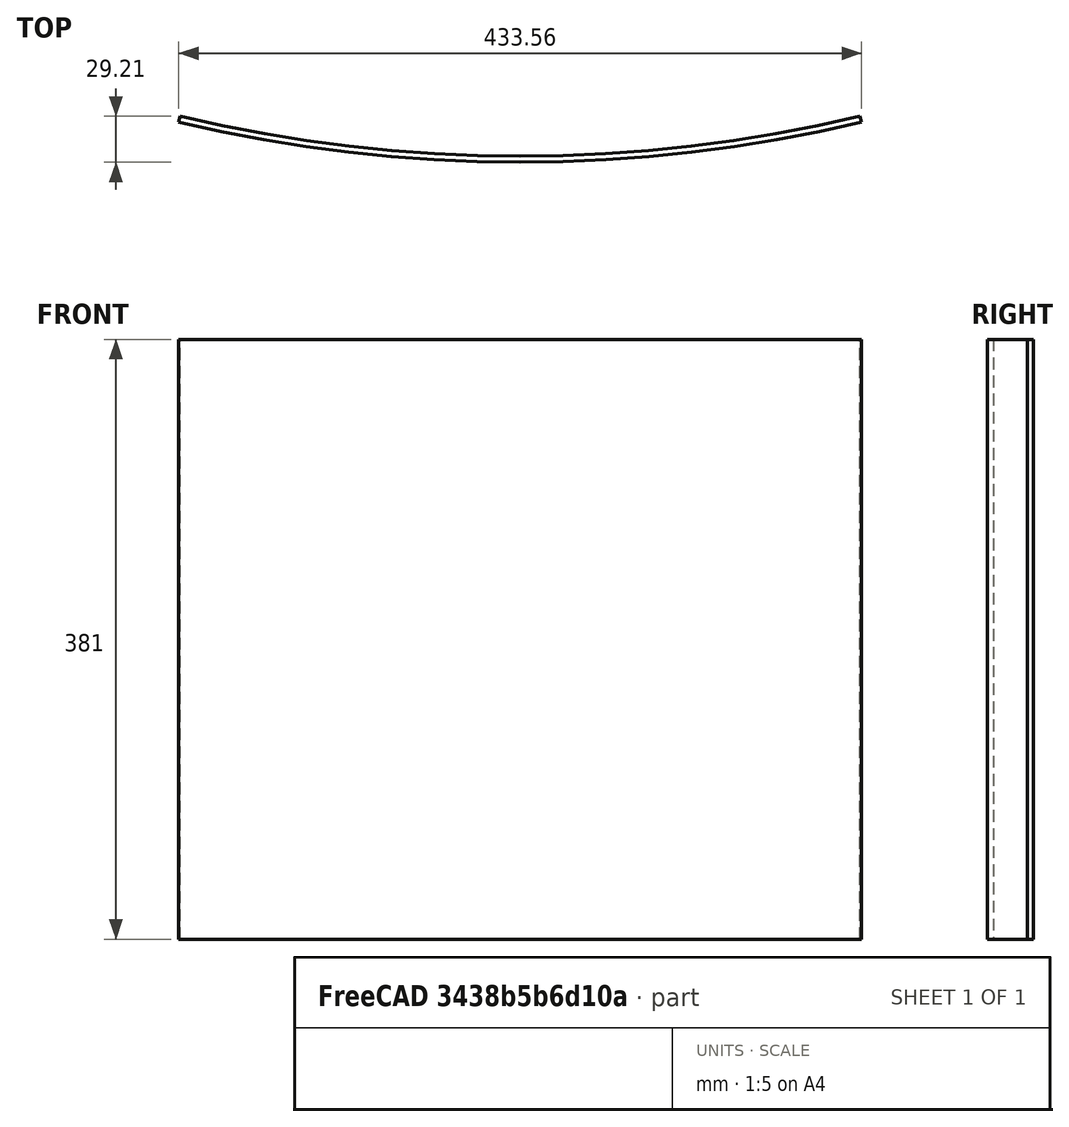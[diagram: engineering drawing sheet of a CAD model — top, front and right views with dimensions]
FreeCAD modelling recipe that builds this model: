
FCSTD DOCUMENT  (FreeCAD 0.21R33345 (Git))
Label: Seat
License: All rights reserved
LicenseURL: http://en.wikipedia.org/wiki/All_rights_reserved
objects: Sketcher::SketchObject×1, PartDesign::Pad×1, PartDesign::Body×1
note: 4 computed .brp shape members not serialized (recipe doc carries the construction recipe); baked Part::Feature solids carry a one-line shape summary decoded from their .brp

FEATURE [Sketcher::SketchObject] Sketch
  FullyConstrained = true
  MapMode = 5
  Support = -> [XY_Plane]
  sketch-geometry (7):
    g0: LineSegment StartX=0 StartY=0 StartZ=0 EndX=0 EndY=25.4 EndZ=0
    g1: LineSegment StartX=-215.9 StartY=25.4 StartZ=0 EndX=215.9 EndY=25.4 EndZ=0
    g2: ArcOfCircle CenterX=-1.6e-15 CenterY=930.275 CenterZ=0 NormalX=0 NormalY=0 NormalZ=1 AngleXU=0 Radius=930.275 StartAngle=4.47817 EndAngle=4.94661
    g3: LineSegment StartX=-215.9 StartY=25.4 StartZ=0 EndX=-216.784 EndY=21.694 EndZ=0
    g4: LineSegment StartX=215.9 StartY=25.4 StartZ=0 EndX=216.784 EndY=21.694 EndZ=0
    g5: LineSegment StartX=0 StartY=0 StartZ=0 EndX=0 EndY=-3.81 EndZ=0
    g6: ArcOfCircle CenterX=1.649e-13 CenterY=930.275 CenterZ=0 NormalX=0 NormalY=0 NormalZ=1 AngleXU=0 Radius=934.085 StartAngle=4.47817 EndAngle=4.94661
  constraints (21):
    c: Coincident(g0,g-1)
    c: PointOnObject(g0,g-2)
    c: PointOnObject(g0,g1)
    c: Symmetric(g1,g1,g0)
    c: DistanceX(g1,g1) = 431.8
    c: Coincident(g2,g1)
    c: Coincident(g2,g1)
    c: PointOnObject(g0,g2)
    c: DistanceY(g0,g0) = 25.4
    c: Coincident(g3,g2)
    c: Coincident(g4,g2)
    c: Perpendicular(g2,g3)
    c: Perpendicular(g2,g4)
    c: Distance(g3) = 3.81
    c: Distance(g4) = 3.81
    c: Coincident(g5,g0)
    c: PointOnObject(g5,g-2)
    c: DistanceY(g5,g5) = 3.81
    c: Coincident(g6,g3)
    c: Coincident(g6,g4)
    c: PointOnObject(g5,g6)
FEATURE [PartDesign::Pad] Pad
  Direction = (0,0,1)
  Length = 381
  Length2 = 10
  Profile = -> Sketch
  ReferenceAxis = -> Sketch [N_Axis]
  Refine = true
  Type = 0
FEATURE [PartDesign::Body] Body
  Group = -> [Sketch,Pad]
  Origin = -> Origin
  Tip = -> Pad
